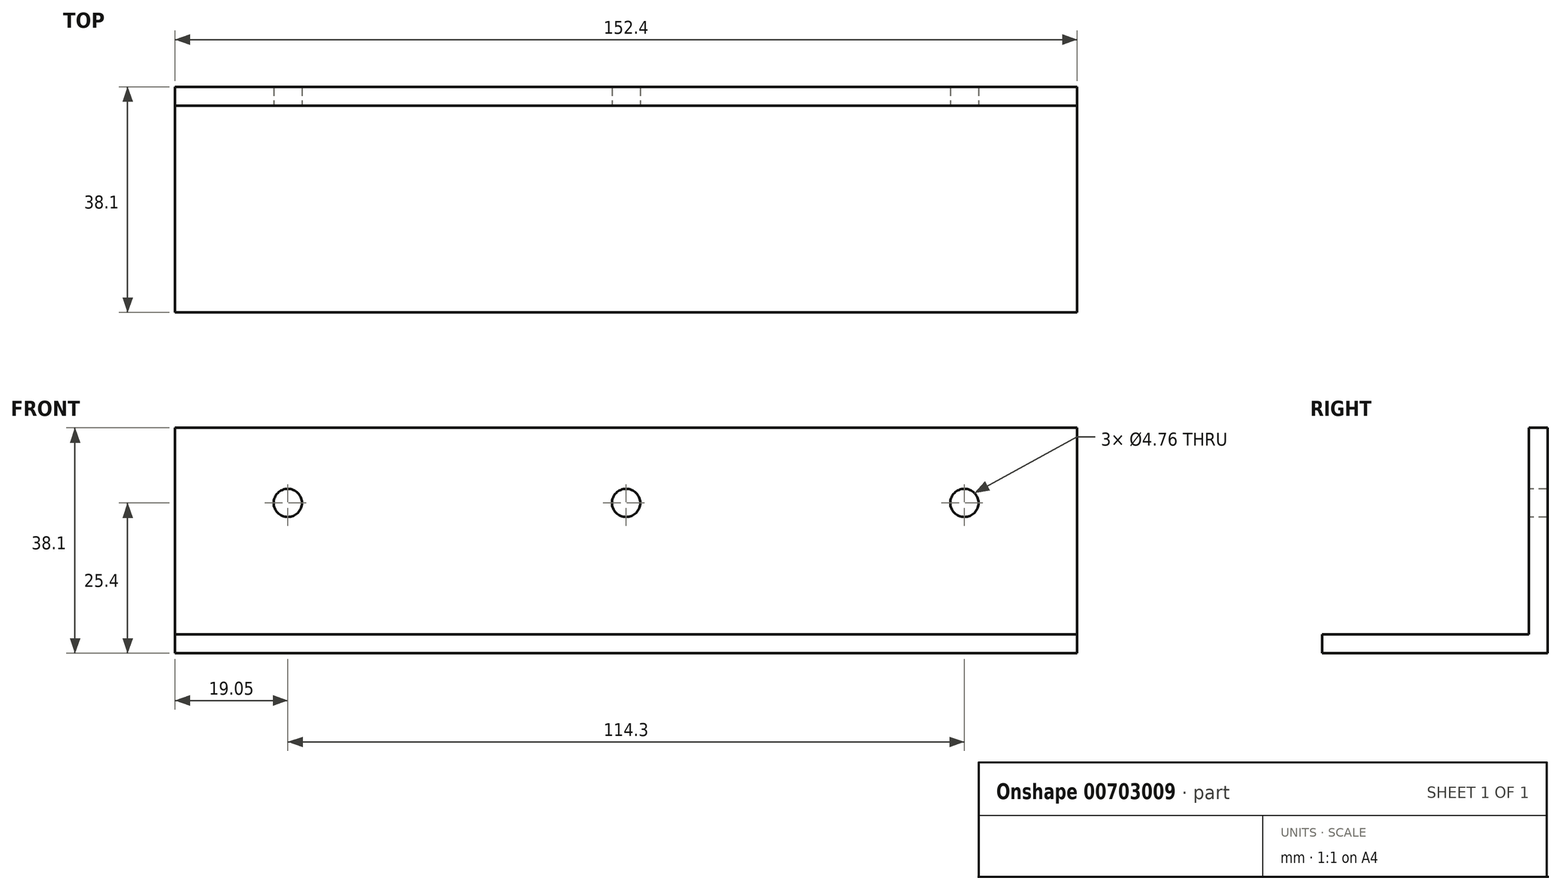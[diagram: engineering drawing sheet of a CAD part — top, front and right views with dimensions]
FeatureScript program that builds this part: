
annotation { "Feature Type Name" : "Feature", "Feature Type Description" : "" }
export const myFeature = defineFeature(function(context is Context, id is Id, definition is map)
    precondition{}
    {
        {
            var Q0;
            Q0=qCreatedBy(makeId("Right.planeOp"),FACE);
            var sketch = newSketch(context, id + "F0", { "sketchPlane" : qUnion([Q0])});
            skLineSegment(sketch, "E0", {"start": v(0, 0) * mm, "end": v(0, 38.1) * mm});
            skLineSegment(sketch, "E1", {"start": v(0, 0) * mm, "end": v(-38.1, 0) * mm});
            skLineSegment(sketch, "E2.0", {"start": v(-3.18, 3.18) * mm, "end": v(-3.18, 38.1) * mm});
            skLineSegment(sketch, "E2.1", {"start": v(-3.18, 3.18) * mm, "end": v(-38.1, 3.17) * mm});
            skLineSegment(sketch, "E3", {"start": v(-3.18, 38.1) * mm, "end": v(0, 38.1) * mm});
            skLineSegment(sketch, "E4", {"start": v(-38.1, 0) * mm, "end": v(-38.1, 3.17) * mm});
            skSolve(sketch);
        }
        {
            var Q0;
            Q0=makeQuery(id+"F0.imprint","IMPRINT",FACE,{"disambiguationData":[TD([[makeQuery(id+"F0.imprint","IMPRINT",EDGE,{"derivedFrom":sQuery(id+"F0.wireOp",EDGE,"E0")}),1.0]])]});
            extrude(context, id + "F1", {"entities" : qUnion([Q0]), "depth" : 152.4 * mm, "offsetDistance" : 25.4 * mm});
        }
        {
            var Q0;
            Q0=makeQuery(id+"F1.opExtrude","SWEPT_FACE",FACE,{"disambiguationData":[OSD([sQuery(id+"F0.wireOp",EDGE,"E2.0")])]});
            var sketch = newSketch(context, id + "F2", { "sketchPlane" : qUnion([Q0])});
            skLineSegment(sketch, "E5", {"start": v(0, 38.1) * mm, "end": v(0, 25.4) * mm});
            skLineSegment(sketch, "E6", {"start": v(0, 25.4) * mm, "end": v(152.4, 25.4) * mm});
            skPoint(sketch, "E7", {"position": v(19.05, 25.4) * mm});
            skPoint(sketch, "E8", {"position": v(76.2, 25.4) * mm});
            skPoint(sketch, "E9", {"position": v(133.35, 25.4) * mm});
            skSolve(sketch);
        }
        {
            var Q0;
            Q0=sQuery(id+"F2.wireOp",VERTEX,"E7");
            var Q1;
            Q1=sQuery(id+"F2.wireOp",VERTEX,"E8");
            var Q2;
            Q2=sQuery(id+"F2.wireOp",VERTEX,"E9");
            var Q3;
            Q3=makeQuery(id+"F1.opExtrude","SWEPT_BODY",BODY,{"disambiguationData":[OSD([sQuery(id+"F0.wireOp",EDGE,"E0"),sQuery(id+"F0.wireOp",EDGE,"E1"),sQuery(id+"F0.wireOp",EDGE,"E2.0"),sQuery(id+"F0.wireOp",EDGE,"E2.1"),sQuery(id+"F0.wireOp",EDGE,"E3"),sQuery(id+"F0.wireOp",EDGE,"E4")])]});
            hole(context, id + "F3", {"style" : HoleStyle.SIMPLE, "endStyle" : HoleEndStyle.THROUGH, "holeDiameter" : 4.76 * mm, "majorDiameter" : 6.35 * mm, "isTappedThrough" : true, "tappedDepth" : 12.7 * mm, "tapClearance" : 3, "locations" : qUnion([Q0, Q1, Q2]), "scope" : qUnion([Q3])});
        }
    });
